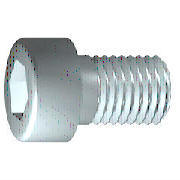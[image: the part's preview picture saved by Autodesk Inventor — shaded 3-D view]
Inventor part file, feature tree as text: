
AUTODESK INVENTOR PART (.ipt)
format: ipt  version: 2022 (Build 260153000, 153)  size: 196,608 bytes
history: native  units: mm (DEFAULTED — no unit token found)
features: sketch x2, other x1, extrude x1, plane x1, fillet x1
ambient origin geometry x7: Origin, YZ Plane, XY Plane, X Axis, Y Axis, Z Axis, Center Point
bodies: Solid1 (feature_tree)
feature tree (6):
  other  "Базовый элемент"
  extrude  "Паз"  Depth=6.875mm
  plane  "Work Plane1"
  fillet  "Fillet2"  Radius=0.276153mm
  sketch  "Эскиз1"
  sketch  "Эскиз2"
